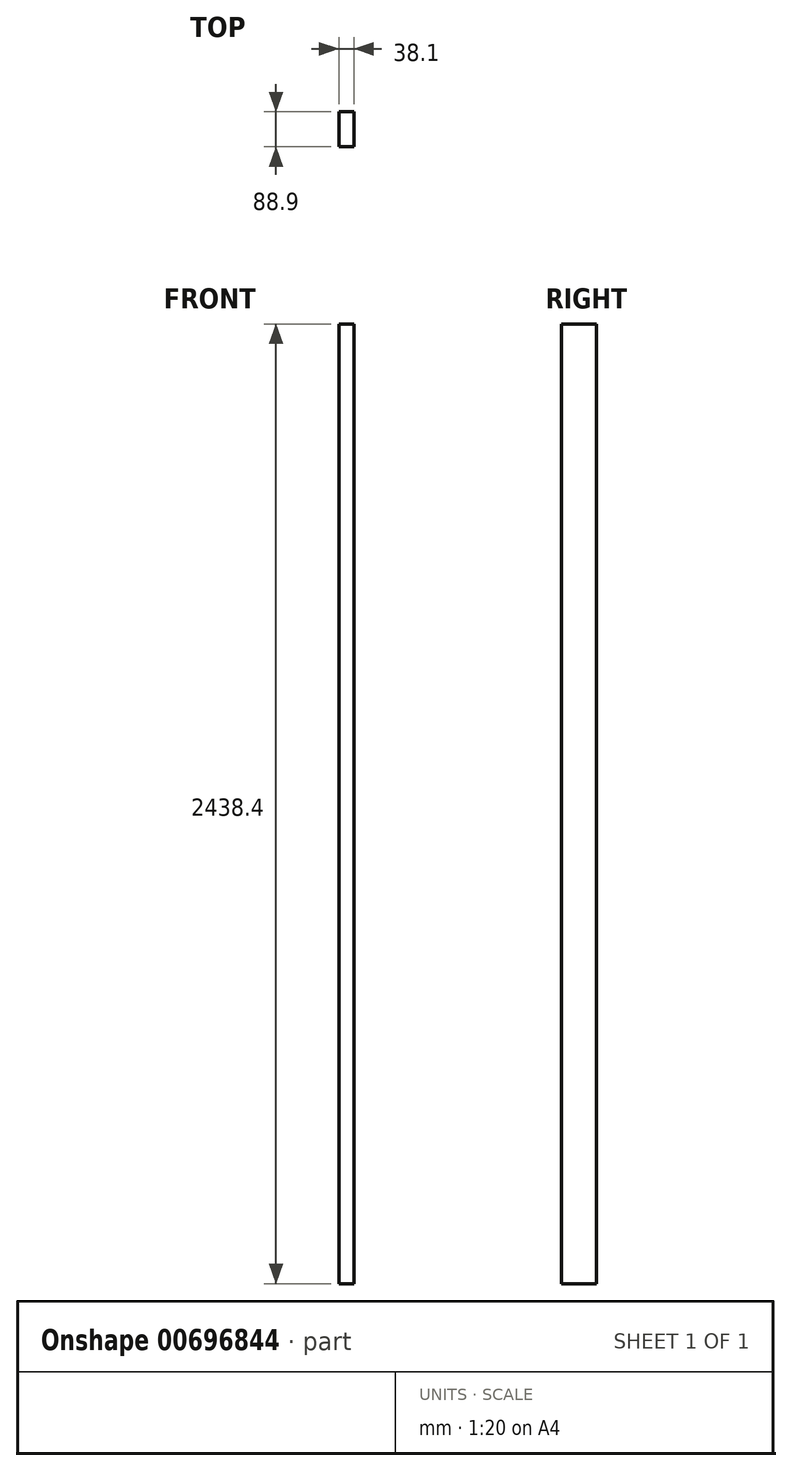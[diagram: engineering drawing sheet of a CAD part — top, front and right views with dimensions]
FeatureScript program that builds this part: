
annotation { "Feature Type Name" : "Feature", "Feature Type Description" : "" }
export const myFeature = defineFeature(function(context is Context, id is Id, definition is map)
    precondition{}
    {
        {
            var Q0;
            Q0=qCreatedBy(makeId("Top.planeOp"),FACE);
            var sketch = newSketch(context, id + "F0", { "sketchPlane" : qUnion([Q0])});
            skLineSegment(sketch, "E0.bottom", {"start": v(0, 0) * mm, "end": v(38.1, 0) * mm});
            skLineSegment(sketch, "E0.top", {"start": v(0, 88.9) * mm, "end": v(38.1, 88.9) * mm});
            skLineSegment(sketch, "E0.left", {"start": v(0, 0) * mm, "end": v(0, 88.9) * mm});
            skLineSegment(sketch, "E0.right", {"start": v(38.1, 0) * mm, "end": v(38.1, 88.9) * mm});
            skSolve(sketch);
        }
        {
            var Q0;
            Q0 = qSketchRegion(id + "F0", true);
            extrude(context, id + "F1", {"entities" : qUnion([Q0]), "depth" : 2438.4 * mm, "offsetDistance" : 25.4 * mm});
        }
    });
